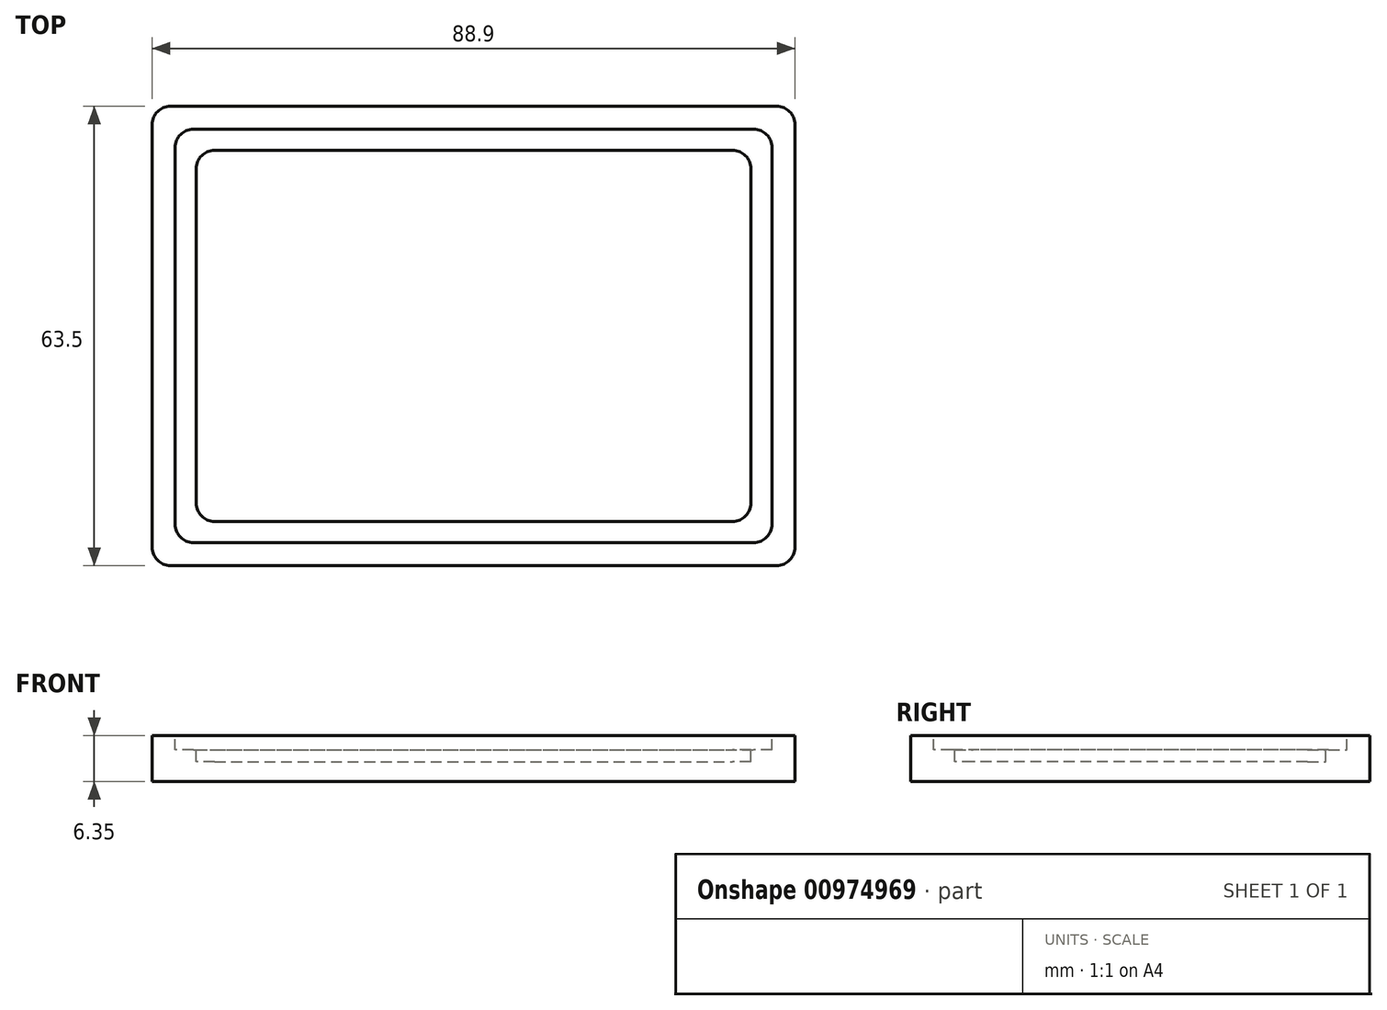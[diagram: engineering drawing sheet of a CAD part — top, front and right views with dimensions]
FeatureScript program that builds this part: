
annotation { "Feature Type Name" : "Feature", "Feature Type Description" : "" }
export const myFeature = defineFeature(function(context is Context, id is Id, definition is map)
    precondition{}
    {
        {
            var Q0;
            Q0=qCreatedBy(makeId("Top.planeOp"),FACE);
            var sketch = newSketch(context, id + "F0", { "sketchPlane" : qUnion([Q0])});
            skLineSegment(sketch, "E0.bottom", {"start": v(-44.45, 31.75) * mm, "end": v(44.45, 31.75) * mm});
            skLineSegment(sketch, "E0.top", {"start": v(-44.45, -31.75) * mm, "end": v(44.45, -31.75) * mm});
            skLineSegment(sketch, "E0.left", {"start": v(-44.45, 31.75) * mm, "end": v(-44.45, -31.75) * mm});
            skLineSegment(sketch, "E0.right", {"start": v(44.45, 31.75) * mm, "end": v(44.45, -31.75) * mm});
            skPoint(sketch, "E0.middle", {"position": v(0, 0) * mm});
            skSolve(sketch);
        }
        {
            var Q0;
            Q0 = qSketchRegion(id + "F0", true);
            extrude(context, id + "F1", {"entities" : qUnion([Q0]), "depth" : 6.35 * mm, "offsetDistance" : 25.4 * mm});
        }
        {
            var Q0;
            Q0=makeQuery(id+"F1.opExtrude","SWEPT_EDGE",EDGE,{"disambiguationData":[OSD([sQuery(id+"F0.wireOp",EDGE,"E0.top"),sQuery(id+"F0.wireOp",EDGE,"E0.left")])]});
            var Q1;
            Q1=makeQuery(id+"F1.opExtrude","SWEPT_EDGE",EDGE,{"disambiguationData":[OSD([sQuery(id+"F0.wireOp",EDGE,"E0.top"),sQuery(id+"F0.wireOp",EDGE,"E0.right")])]});
            var Q2;
            Q2=makeQuery(id+"F1.opExtrude","SWEPT_EDGE",EDGE,{"disambiguationData":[OSD([sQuery(id+"F0.wireOp",EDGE,"E0.bottom"),sQuery(id+"F0.wireOp",EDGE,"E0.right")])]});
            var Q3;
            Q3=makeQuery(id+"F1.opExtrude","SWEPT_EDGE",EDGE,{"disambiguationData":[OSD([sQuery(id+"F0.wireOp",EDGE,"E0.bottom"),sQuery(id+"F0.wireOp",EDGE,"E0.left")])]});
            fillet(context, id + "F2", {"entities" : qUnion([Q0, Q1, Q2, Q3]), "radius" : 2.54 * mm, "tangentPropagation" : true, "allowEdgeOverflow" : false});
        }
        {
            var Q0;
            Q0=makeQuery(id+"F1.opExtrude","CAP_FACE",FACE,{"disambiguationData":[OSD([sQuery(id+"F0.wireOp",EDGE,"E0.bottom"),sQuery(id+"F0.wireOp",EDGE,"E0.top"),sQuery(id+"F0.wireOp",EDGE,"E0.left"),sQuery(id+"F0.wireOp",EDGE,"E0.right")])],"isStart":false});
            var sketch = newSketch(context, id + "F3", { "sketchPlane" : qUnion([Q0])});
            skLineSegment(sketch, "E1.bottom", {"start": v(-38.73, 28.57) * mm, "end": v(38.74, 28.57) * mm});
            skLineSegment(sketch, "E1.top", {"start": v(-38.74, -28.57) * mm, "end": v(38.73, -28.57) * mm});
            skLineSegment(sketch, "E1.left", {"start": v(-41.27, 26.04) * mm, "end": v(-41.28, -26.04) * mm});
            skLineSegment(sketch, "E1.right", {"start": v(41.28, 26.04) * mm, "end": v(41.27, -26.04) * mm});
            skPoint(sketch, "E1.middle", {"position": v(0, 0) * mm});
            skPoint(sketch, "E2.visualSharp", {"position": v(-41.27, 28.57) * mm});
            skArc(sketch, "E2.filletArc", {"start": v(-38.73, 28.58) * mm, "mid": v(-40.53, 27.83) * mm, "end": v(-41.27, 26.04) * mm});
            skPoint(sketch, "E3.visualSharp", {"position": v(41.28, 28.57) * mm});
            skArc(sketch, "E3.filletArc", {"start": v(41.28, 26.04) * mm, "mid": v(40.53, 27.83) * mm, "end": v(38.74, 28.57) * mm});
            skPoint(sketch, "E4.visualSharp", {"position": v(41.27, -28.57) * mm});
            skArc(sketch, "E4.filletArc", {"start": v(38.73, -28.57) * mm, "mid": v(40.53, -27.83) * mm, "end": v(41.28, -26.04) * mm});
            skPoint(sketch, "E5.visualSharp", {"position": v(-41.28, -28.57) * mm});
            skArc(sketch, "E5.filletArc", {"start": v(-41.28, -26.04) * mm, "mid": v(-40.53, -27.83) * mm, "end": v(-38.74, -28.57) * mm});
            skSolve(sketch);
        }
        {
            var Q0;
            Q0 = qSketchRegion(id + "F3", true);
            extrude(context, id + "F4", {"entities" : qUnion([Q0]), "operationType" : NewBodyOperationType.REMOVE, "oppositeDirection" : true, "depth" : 2 * mm, "offsetDistance" : 25.4 * mm});
        }
        {
            var Q0;
            Q0=makeQuery(id+"F4.boolean.opBoolean","COPY",FACE,{"derivedFrom":makeQuery(id+"F4.opExtrude","CAP_FACE",FACE,{"disambiguationData":[OSD([sQuery(id+"F3.wireOp",EDGE,"E1.bottom"),sQuery(id+"F3.wireOp",EDGE,"E1.top"),sQuery(id+"F3.wireOp",EDGE,"E1.left"),sQuery(id+"F3.wireOp",EDGE,"E1.right"),sQuery(id+"F3.wireOp",EDGE,"E2.filletArc"),sQuery(id+"F3.wireOp",EDGE,"E3.filletArc"),sQuery(id+"F3.wireOp",EDGE,"E4.filletArc"),sQuery(id+"F3.wireOp",EDGE,"E5.filletArc")])],"isStart":false})});
            var sketch = newSketch(context, id + "F5", { "sketchPlane" : qUnion([Q0])});
            skLineSegment(sketch, "E6.bottom", {"start": v(-35.81, 25.65) * mm, "end": v(35.81, 25.65) * mm});
            skLineSegment(sketch, "E6.top", {"start": v(-35.81, -25.65) * mm, "end": v(35.81, -25.65) * mm});
            skLineSegment(sketch, "E6.left", {"start": v(-38.35, 23.11) * mm, "end": v(-38.35, -23.11) * mm});
            skLineSegment(sketch, "E6.right", {"start": v(38.35, 23.11) * mm, "end": v(38.35, -23.11) * mm});
            skPoint(sketch, "E6.middle", {"position": v(0, 0) * mm});
            skPoint(sketch, "E7.visualSharp", {"position": v(-38.35, 25.65) * mm});
            skArc(sketch, "E7.filletArc", {"start": v(-35.81, 25.65) * mm, "mid": v(-37.61, 24.91) * mm, "end": v(-38.35, 23.11) * mm});
            skPoint(sketch, "E8.visualSharp", {"position": v(38.35, 25.65) * mm});
            skArc(sketch, "E8.filletArc", {"start": v(38.35, 23.11) * mm, "mid": v(37.61, 24.91) * mm, "end": v(35.81, 25.65) * mm});
            skPoint(sketch, "E9.visualSharp", {"position": v(38.35, -25.65) * mm});
            skArc(sketch, "E9.filletArc", {"start": v(35.81, -25.65) * mm, "mid": v(37.61, -24.91) * mm, "end": v(38.35, -23.11) * mm});
            skPoint(sketch, "E10.visualSharp", {"position": v(-38.35, -25.65) * mm});
            skArc(sketch, "E10.filletArc", {"start": v(-38.35, -23.11) * mm, "mid": v(-37.61, -24.91) * mm, "end": v(-35.81, -25.65) * mm});
            skSolve(sketch);
        }
        {
            var Q0;
            Q0 = qSketchRegion(id + "F5", true);
            extrude(context, id + "F6", {"entities" : qUnion([Q0]), "operationType" : NewBodyOperationType.REMOVE, "oppositeDirection" : true, "depth" : 1.63 * mm, "offsetDistance" : 25.4 * mm});
        }
    });
